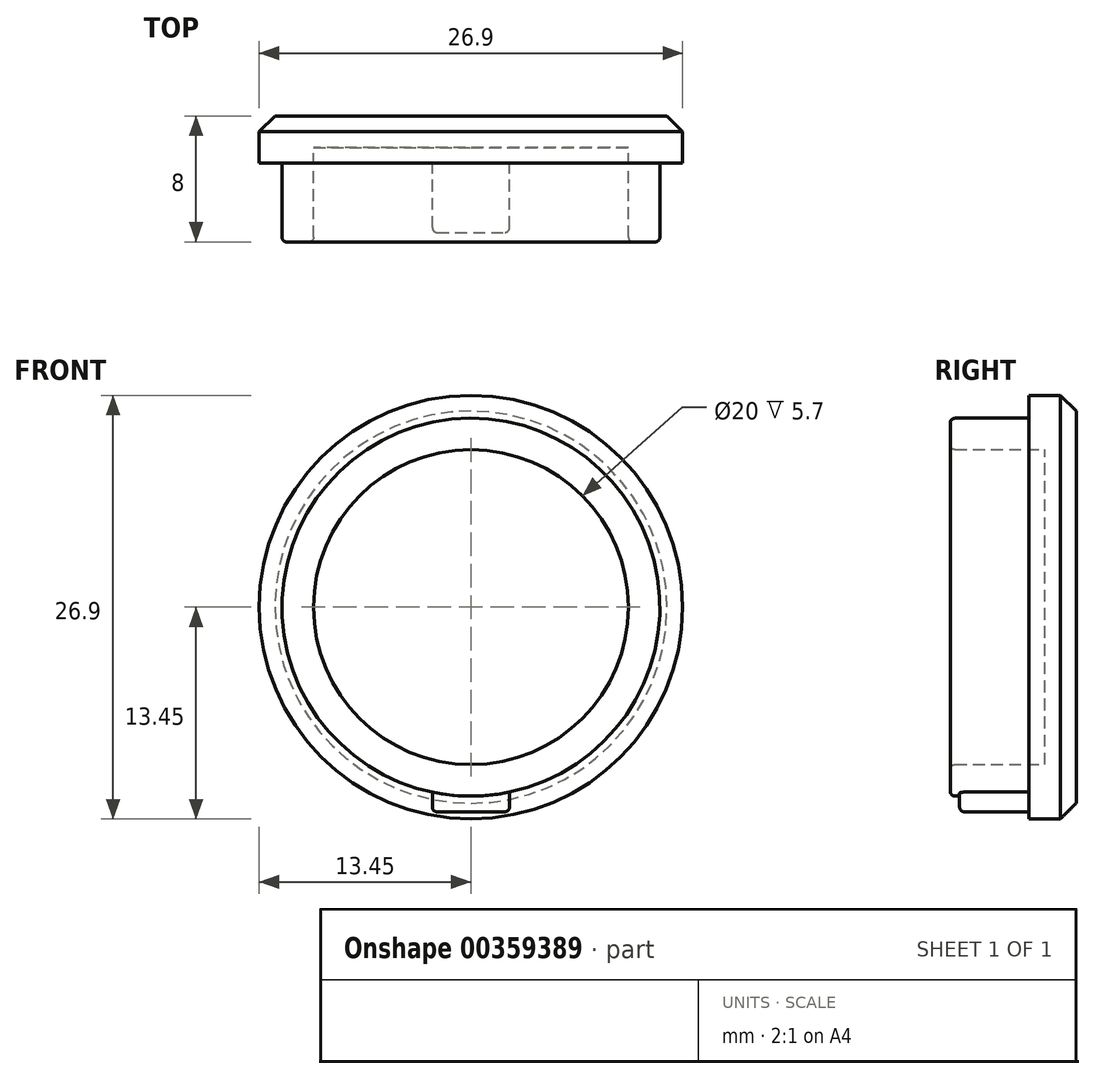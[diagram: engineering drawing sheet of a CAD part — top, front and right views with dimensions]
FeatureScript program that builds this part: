
annotation { "Feature Type Name" : "Feature", "Feature Type Description" : "" }
export const myFeature = defineFeature(function(context is Context, id is Id, definition is map)
    precondition{}
    {
        {
            var Q0;
            Q0=qCreatedBy(makeId("Front.planeOp"),FACE);
            var sketch = newSketch(context, id + "F0", { "sketchPlane" : qUnion([Q0])});
            skCircle(sketch, "E0", {"center": v(0, 0) * mm, "radius": 12 * mm});
            skCircle(sketch, "E1", {"center": v(0, 0) * mm, "radius": 10 * mm});
            skSolve(sketch);
        }
        {
            var Q0;
            Q0=makeQuery(id+"F0.imprint","IMPRINT",FACE,{"disambiguationData":[TD([[makeQuery(id+"F0.imprint","IMPRINT",EDGE,{"derivedFrom":sQuery(id+"F0.wireOp",EDGE,"E0")}),1.0]])]});
            extrude(context, id + "F1", {"entities" : qUnion([Q0]), "depth" : 6 * mm});
        }
        {
            var Q0;
            Q0=qCreatedBy(makeId("Front.planeOp"),FACE);
            var sketch = newSketch(context, id + "F2", { "sketchPlane" : qUnion([Q0])});
            skCircle(sketch, "E2", {"center": v(0, 0) * mm, "radius": 13.45 * mm});
            skSolve(sketch);
        }
        {
            var Q0;
            Q0 = qSketchRegion(id + "F2", true);
            extrude(context, id + "F3", {"entities" : qUnion([Q0]), "operationType" : NewBodyOperationType.ADD, "depth" : 1 * mm, "hasSecondDirection" : true, "secondDirectionOppositeDirection" : true, "secondDirectionDepth" : 2 * mm});
        }
        {
            var Q0;
            Q0=qCreatedBy(makeId("Front.planeOp"),FACE);
            var sketch = newSketch(context, id + "F4", { "sketchPlane" : qUnion([Q0])});
            skCircle(sketch, "E3", {"center": v(0, 0) * mm, "radius": 10 * mm});
            skSolve(sketch);
        }
        {
            var Q0;
            Q0 = qSketchRegion(id + "F4", true);
            var Q1;
            Q1=makeQuery(id+"F1.opExtrude","CAP_FACE",FACE,{"disambiguationData":[OSD([sQuery(id+"F0.wireOp",EDGE,"E0"),sQuery(id+"F0.wireOp",EDGE,"E1")])],"isStart":false});
            extrude(context, id + "F5", {"entities" : qUnion([Q0]), "operationType" : NewBodyOperationType.REMOVE, "endBound" : BoundingType.UP_TO_SURFACE, "endBoundEntityFace" : qUnion([Q1]), "depth" : 25 * mm});
        }
        {
            var Q0;
            Q0=qCreatedBy(makeId("Front.planeOp"),FACE);
            var sketch = newSketch(context, id + "F6", { "sketchPlane" : qUnion([Q0])});
            skLineSegment(sketch, "E4.bottom", {"start": v(-2.45, -11) * mm, "end": v(2.45, -11) * mm});
            skLineSegment(sketch, "E4.top", {"start": v(-2.45, -13) * mm, "end": v(2.45, -13) * mm});
            skLineSegment(sketch, "E4.left", {"start": v(-2.45, -11) * mm, "end": v(-2.45, -13) * mm});
            skLineSegment(sketch, "E4.right", {"start": v(2.45, -11) * mm, "end": v(2.45, -13) * mm});
            skSolve(sketch);
        }
        {
            var Q0;
            Q0 = qSketchRegion(id + "F6", true);
            extrude(context, id + "F7", {"entities" : qUnion([Q0]), "operationType" : NewBodyOperationType.ADD, "depth" : 5.4 * mm});
        }
        {
            var Q0;
            Q0=makeQuery(id+"F3.opExtrude","CAP_EDGE",EDGE,{"disambiguationData":[OSD([sQuery(id+"F2.wireOp",EDGE,"E2")])],"isStart":true});
            chamfer(context, id + "F8", {"entities" : qUnion([Q0]), "width" : 1 * mm, "tangentPropagation" : true});
        }
        {
            var Q0;
            Q0=makeQuery(id+"F7.opExtrude","SWEPT_EDGE",EDGE,{"disambiguationData":[OSD([sQuery(id+"F6.wireOp",EDGE,"E4.top"),sQuery(id+"F6.wireOp",EDGE,"E4.left")])]});
            var Q1;
            Q1=makeQuery(id+"F7.opExtrude","CAP_EDGE",EDGE,{"disambiguationData":[OSD([sQuery(id+"F6.wireOp",EDGE,"E4.top")])],"isStart":false});
            var Q2;
            Q2=makeQuery(id+"F7.opExtrude","SWEPT_EDGE",EDGE,{"disambiguationData":[OSD([sQuery(id+"F6.wireOp",EDGE,"E4.top"),sQuery(id+"F6.wireOp",EDGE,"E4.right")])]});
            var Q3;
            Q3=makeQuery(id+"F7.opExtrude","CAP_EDGE",EDGE,{"disambiguationData":[OSD([sQuery(id+"F6.wireOp",EDGE,"E4.left")])],"isStart":false});
            var Q4;
            Q4=makeQuery(id+"F7.opExtrude","CAP_EDGE",EDGE,{"disambiguationData":[OSD([sQuery(id+"F6.wireOp",EDGE,"E4.right")])],"isStart":false});
            fillet(context, id + "F9", {"entities" : qUnion([Q0, Q1, Q2, Q3, Q4]), "radius" : .3 * mm, "tangentPropagation" : true, "allowEdgeOverflow" : false});
        }
        {
            var Q0;
            Q0=makeQuery(id+"F1.opExtrude","CAP_EDGE",EDGE,{"disambiguationData":[OSD([sQuery(id+"F0.wireOp",EDGE,"E0")])],"isStart":false});
            var Q1;
            Q1=makeQuery(id+"F1.opExtrude","CAP_EDGE",EDGE,{"disambiguationData":[OSD([sQuery(id+"F0.wireOp",EDGE,"E1")])],"isStart":false});
            fillet(context, id + "F10", {"entities" : qUnion([Q0, Q1]), "radius" : .3 * mm, "tangentPropagation" : true, "allowEdgeOverflow" : false});
        }
    });
